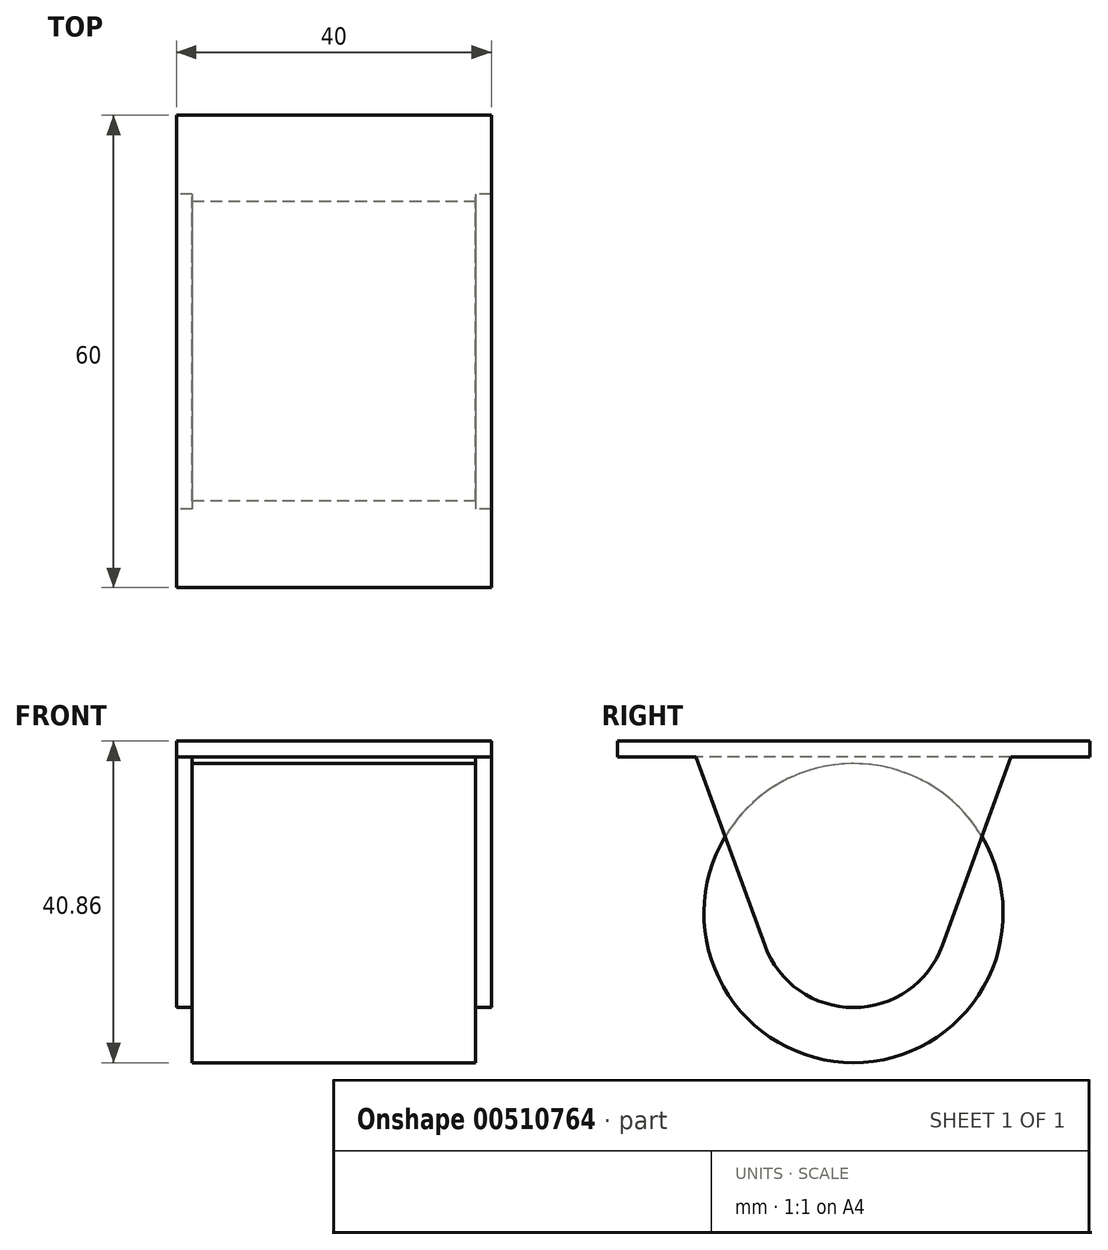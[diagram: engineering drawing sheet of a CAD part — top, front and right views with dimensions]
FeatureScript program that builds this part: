
annotation { "Feature Type Name" : "Feature", "Feature Type Description" : "" }
export const myFeature = defineFeature(function(context is Context, id is Id, definition is map)
    precondition{}
    {
        {
            var Q0;
            Q0=qCreatedBy(makeId("Top.planeOp"),FACE);
            var sketch = newSketch(context, id + "F0", { "sketchPlane" : qUnion([Q0])});
            skLineSegment(sketch, "E0.bottom", {"start": v(-20, 30) * mm, "end": v(20, 30) * mm});
            skLineSegment(sketch, "E0.top", {"start": v(-20, -30) * mm, "end": v(20, -30) * mm});
            skLineSegment(sketch, "E0.left", {"start": v(-20, 30) * mm, "end": v(-20, -30) * mm});
            skLineSegment(sketch, "E0.right", {"start": v(20, 30) * mm, "end": v(20, -30) * mm});
            skPoint(sketch, "E0.middle", {"position": v(0, 0) * mm});
            skSolve(sketch);
        }
        {
            var Q0;
            Q0=makeQuery(id+"F0.imprint","IMPRINT",FACE,{"disambiguationData":[TD([[makeQuery(id+"F0.imprint","IMPRINT",EDGE,{"derivedFrom":sQuery(id+"F0.wireOp",EDGE,"E0.bottom")}),-1.0]])]});
            extrude(context, id + "F1", {"entities" : qUnion([Q0]), "oppositeDirection" : true, "depth" : 2 * mm, "offsetDistance" : 25 * mm});
        }
        {
            var Q0;
            Q0=qCreatedBy(makeId("Right.planeOp"),FACE);
            var sketch = newSketch(context, id + "F2", { "sketchPlane" : qUnion([Q0])});
            skLineSegment(sketch, "E1.0", {"start": v(30, -2) * mm, "end": v(-30, -2) * mm});
            skLineSegment(sketch, "E2", {"start": v(-20, -2) * mm, "end": v(-11.28, -25.97) * mm});
            skLineSegment(sketch, "E3", {"start": v(20, -2) * mm, "end": v(11.28, -25.97) * mm});
            skArc(sketch, "E4", {"start": v(-11.28, -25.97) * mm, "mid": v(0, -33.86) * mm, "end": v(11.28, -25.97) * mm});
            skSolve(sketch);
        }
        {
            var Q0;
            {var subQ0=sQuery(id+"F2.wireOp",EDGE,"E2");Q0=makeQuery(id+"F2.imprint","IMPRINT",FACE,{"disambiguationData":[TD([[makeQuery(id+"F2.imprint","IMPRINT",EDGE,{"derivedFrom":subQ0}),1.0]])]});}
            extrude(context, id + "F3", {"entities" : qUnion([Q0]), "operationType" : NewBodyOperationType.ADD, "endBound" : BoundingType.SYMMETRIC, "depth" : 40 * mm, "offsetDistance" : 25 * mm});
        }
        {
            var Q0;
            Q0=qCreatedBy(makeId("Front.planeOp"),FACE);
            var sketch = newSketch(context, id + "F4", { "sketchPlane" : qUnion([Q0])});
            skLineSegment(sketch, "E5.0", {"start": v(-20, -2) * mm, "end": v(20, -2) * mm});
            skLineSegment(sketch, "E6", {"start": v(0, -2) * mm, "end": v(0, -54.48) * mm, "construction": true});
            skPoint(sketch, "E6.endSnap0", {"position": v(0, -2) * mm});
            skLineSegment(sketch, "E7", {"start": v(18, -2) * mm, "end": v(18, -42) * mm});
            skLineSegment(sketch, "E8.MirrorCS", {"start": v(-18, -2) * mm, "end": v(-18, -42) * mm});
            skLineSegment(sketch, "E9", {"start": v(18, -42) * mm, "end": v(-18, -42) * mm});
            skSolve(sketch);
        }
        {
            var Q0;
            {var subQ0=sQuery(id+"F4.wireOp",EDGE,"E7");Q0=makeQuery(id+"F4.imprint","IMPRINT",FACE,{"disambiguationData":[TD([[makeQuery(id+"F4.imprint","IMPRINT",EDGE,{"derivedFrom":subQ0}),-1.0]])]});}
            extrude(context, id + "F5", {"entities" : qUnion([Q0]), "operationType" : NewBodyOperationType.REMOVE, "endBound" : BoundingType.SYMMETRIC, "oppositeDirection" : true, "depth" : 40 * mm, "offsetDistance" : 25 * mm});
        }
        {
            var Q0;
            Q0=makeQuery(id+"F5.boolean.opBoolean","COPY",FACE,{"derivedFrom":makeQuery(id+"F5.opExtrude","SWEPT_FACE",FACE,{"disambiguationData":[OSD([sQuery(id+"F4.wireOp",EDGE,"E8.MirrorCS")])]})});
            var sketch = newSketch(context, id + "F6", { "sketchPlane" : qUnion([Q0])});
            skPoint(sketch, "E10.0", {"position": v(0, -21.86) * mm});
            skCircle(sketch, "E11", {"center": v(0, -21.86) * mm, "radius": 19 * mm});
            skSolve(sketch);
        }
        {
            var Q0;
            {var subQ1=makeQuery(id+"F5.opExtrude","SWEPT_FACE",FACE,{"disambiguationData":[OSD([sQuery(id+"F4.wireOp",EDGE,"E8.MirrorCS")])]});var subQ6=makeQuery(id+"F5.boolean.opBoolean","INTERSECT",EDGE,{"derivedFrom":[makeQuery(id+"F3.opExtrude","SWEPT_FACE",FACE,{"disambiguationData":[OSD([sQuery(id+"F2.wireOp",EDGE,"E4")])]}),subQ1]});Q0=makeQuery(id+"F6.imprint","IMPRINT",FACE,{"disambiguationData":[TD([[makeQuery(id+"F6.imprint","IMPRINT",EDGE,{"derivedFrom":subQ6}),-1.0]])]});}
            var Q1;
            {var subQ1=makeQuery(id+"F5.opExtrude","SWEPT_FACE",FACE,{"disambiguationData":[OSD([sQuery(id+"F4.wireOp",EDGE,"E8.MirrorCS")])]});var subQ6=makeQuery(id+"F5.boolean.opBoolean","INTERSECT",EDGE,{"derivedFrom":[makeQuery(id+"F3.opExtrude","SWEPT_FACE",FACE,{"disambiguationData":[OSD([sQuery(id+"F2.wireOp",EDGE,"E4")])]}),subQ1]});Q1=makeQuery(id+"F6.imprint","IMPRINT",FACE,{"disambiguationData":[TD([[makeQuery(id+"F6.imprint","IMPRINT",EDGE,{"derivedFrom":subQ6}),1.0]])]});}
            var Q2;
            Q2=makeQuery(id+"F5.boolean.opBoolean","COPY",VERTEX,{"derivedFrom":makeQuery(id+"F5.opExtrude","CAP_VERTEX",VERTEX,{"disambiguationData":[OSD([sQuery(id+"F4.wireOp",EDGE,"E5.0"),sQuery(id+"F4.wireOp",EDGE,"E7")])],"isStart":false})});
            extrude(context, id + "F7", {"entities" : qUnion([Q0, Q1]), "endBound" : BoundingType.UP_TO_VERTEX, "depth" : 25 * mm, "endBoundEntityVertex" : qUnion([Q2]), "offsetDistance" : 25 * mm});
        }
    });
